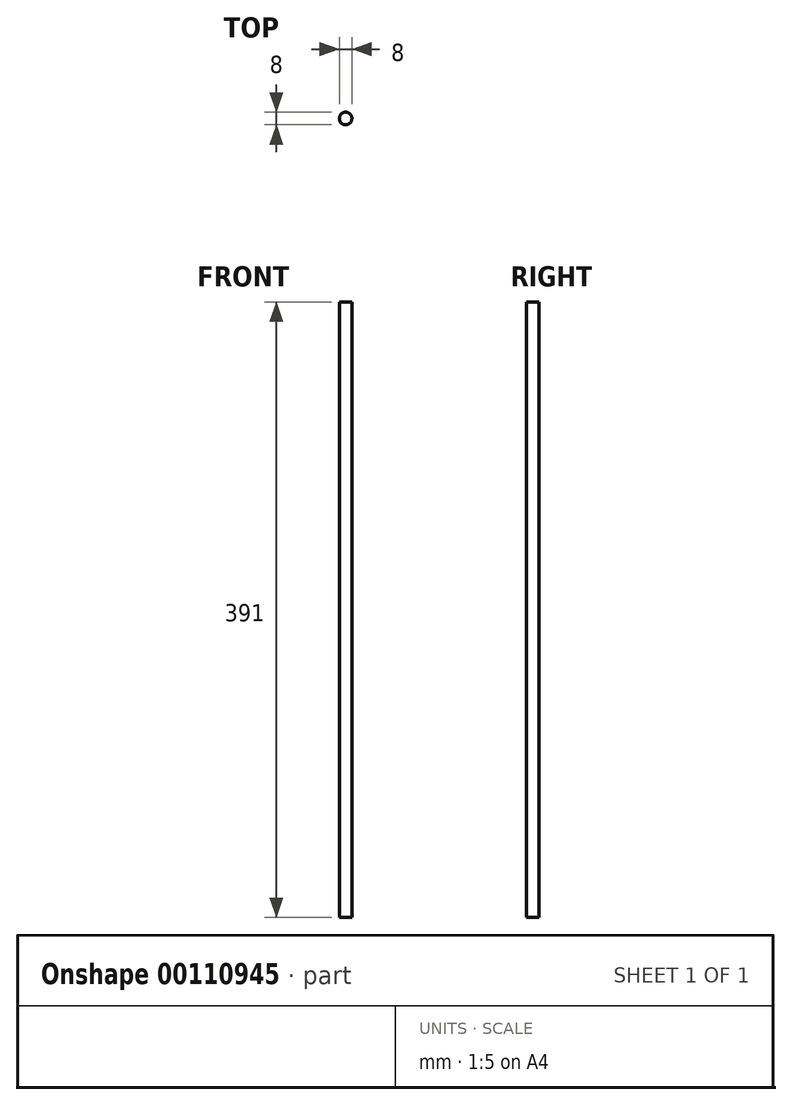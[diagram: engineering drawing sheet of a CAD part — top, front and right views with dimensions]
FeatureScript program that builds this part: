
annotation { "Feature Type Name" : "Feature", "Feature Type Description" : "" }
export const myFeature = defineFeature(function(context is Context, id is Id, definition is map)
    precondition{}
    {
        {
            var Q0;
            Q0=qCreatedBy(makeId("Top.planeOp"),FACE);
            var sketch = newSketch(context, id + "F0", { "sketchPlane" : qUnion([Q0])});
            skCircle(sketch, "E0", {"center": v(0, 0) * mm, "radius": 4 * mm});
            skSolve(sketch);
        }
        {
            var Q0;
            Q0=qSketchRegion(id+"F0",true);
            extrude(context, id + "F1", {"entities" : qUnion([Q0]), "depth" : 391 * mm});
        }
    });
